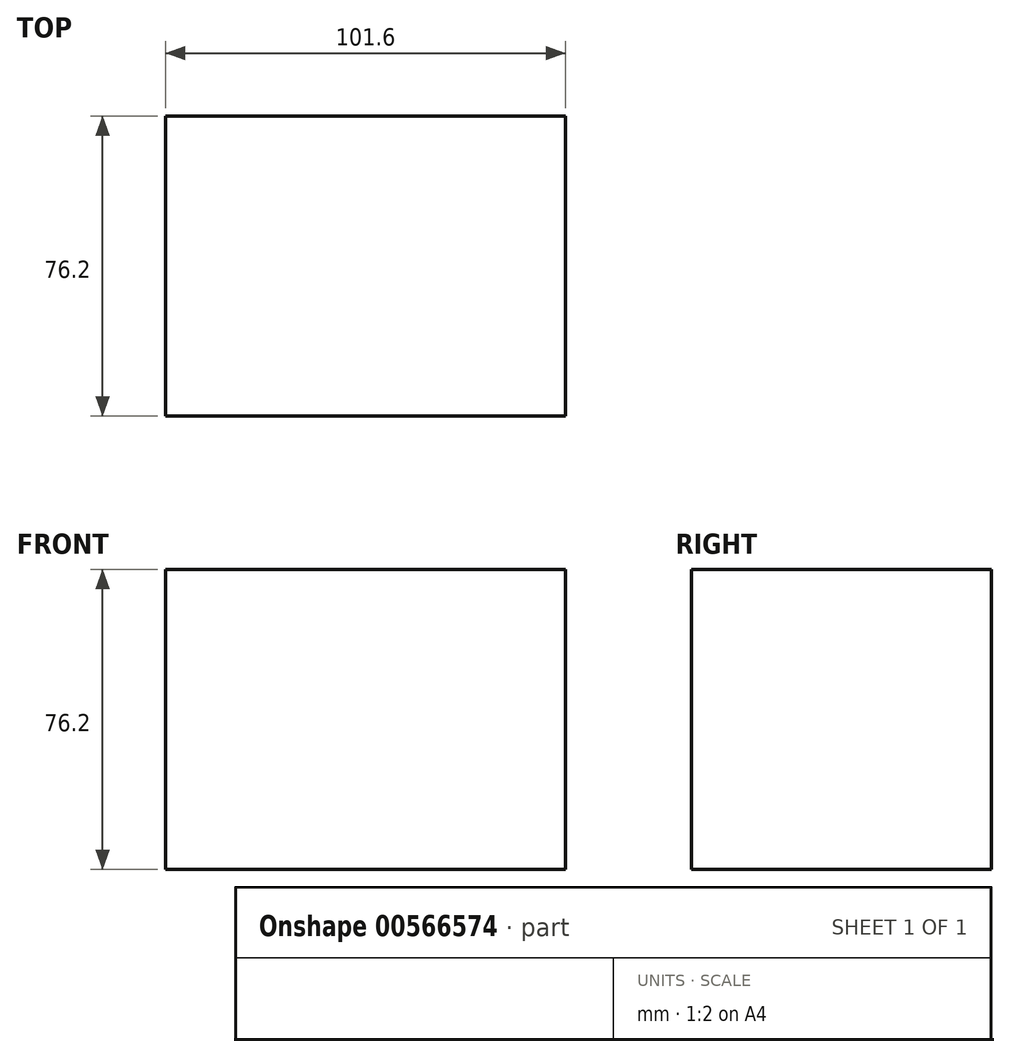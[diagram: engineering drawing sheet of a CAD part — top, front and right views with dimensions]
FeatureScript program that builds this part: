
annotation { "Feature Type Name" : "Feature", "Feature Type Description" : "" }
export const myFeature = defineFeature(function(context is Context, id is Id, definition is map)
    precondition{}
    {
        {
            var Q0;
            Q0=qCreatedBy(makeId("Top.planeOp"),FACE);
            var sketch = newSketch(context, id + "F0", { "sketchPlane" : qUnion([Q0])});
            skLineSegment(sketch, "E0.bottom", {"start": v(50.8, 38.1) * mm, "end": v(-50.8, 38.1) * mm});
            skLineSegment(sketch, "E0.top", {"start": v(50.8, -38.1) * mm, "end": v(-50.8, -38.1) * mm});
            skLineSegment(sketch, "E0.left", {"start": v(50.8, 38.1) * mm, "end": v(50.8, -38.1) * mm});
            skLineSegment(sketch, "E0.right", {"start": v(-50.8, 38.1) * mm, "end": v(-50.8, -38.1) * mm});
            skPoint(sketch, "E0.middle", {"position": v(0, 0) * mm});
            skSolve(sketch);
        }
        {
            var Q0;
            Q0=makeQuery(id+"F0.imprint","IMPRINT",FACE,{"disambiguationData":[TD([[makeQuery(id+"F0.imprint","IMPRINT",EDGE,{"derivedFrom":sQuery(id+"F0.wireOp",EDGE,"E0.bottom")}),1.0]])]});
            extrude(context, id + "F1", {"entities" : qUnion([Q0]), "depth" : 76.2 * mm, "offsetDistance" : 25.4 * mm});
        }
    });
